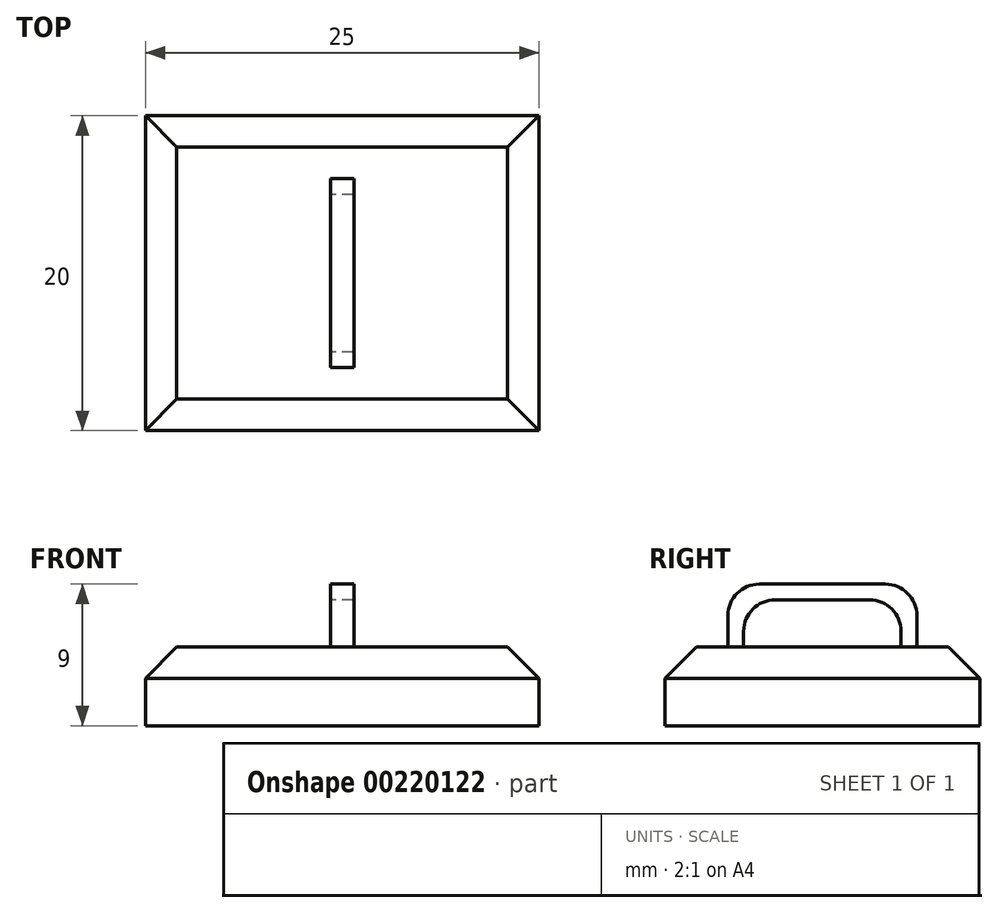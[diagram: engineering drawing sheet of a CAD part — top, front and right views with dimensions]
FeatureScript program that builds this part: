
annotation { "Feature Type Name" : "Feature", "Feature Type Description" : "" }
export const myFeature = defineFeature(function(context is Context, id is Id, definition is map)
    precondition{}
    {
        {
            var Q0;
            Q0=qCreatedBy(makeId("Top.planeOp"),FACE);
            var sketch = newSketch(context, id + "F0", { "sketchPlane" : qUnion([Q0])});
            skLineSegment(sketch, "E0.bottom", {"start": v(12.5, -10) * mm, "end": v(-12.5, -10) * mm});
            skLineSegment(sketch, "E0.top", {"start": v(12.5, 10) * mm, "end": v(-12.5, 10) * mm});
            skLineSegment(sketch, "E0.left", {"start": v(12.5, -10) * mm, "end": v(12.5, 10) * mm});
            skLineSegment(sketch, "E0.right", {"start": v(-12.5, -10) * mm, "end": v(-12.5, 10) * mm});
            skPoint(sketch, "E0.middle", {"position": v(0, 0) * mm});
            skSolve(sketch);
        }
        {
            var Q0;
            Q0 = qSketchRegion(id + "F0", true);
            extrude(context, id + "F1", {"entities" : qUnion([Q0]), "oppositeDirection" : true, "depth" : 5 * mm});
        }
        {
            var Q0;
            Q0=qCreatedBy(makeId("Right.planeOp"),FACE);
            var sketch = newSketch(context, id + "F2", { "sketchPlane" : qUnion([Q0])});
            skLineSegment(sketch, "E1", {"start": v(-6, 0) * mm, "end": v(-6, 4) * mm});
            skLineSegment(sketch, "E2", {"start": v(-5, 3) * mm, "end": v(-5, 0) * mm});
            skLineSegment(sketch, "E3", {"start": v(-5, 0) * mm, "end": v(-6, 0) * mm});
            skLineSegment(sketch, "E4.MirrorCS", {"start": v(6, 0) * mm, "end": v(6, 4) * mm});
            skLineSegment(sketch, "E5.MirrorCS", {"start": v(5, 3) * mm, "end": v(5, 0) * mm});
            skLineSegment(sketch, "E6", {"start": v(-6, 4) * mm, "end": v(6, 4) * mm});
            skLineSegment(sketch, "E7", {"start": v(-5, 3) * mm, "end": v(5, 3) * mm});
            skLineSegment(sketch, "E8", {"start": v(5, 0) * mm, "end": v(6, 0) * mm});
            skSolve(sketch);
        }
        {
            var Q0;
            Q0 = qSketchRegion(id + "F2", true);
            extrude(context, id + "F3", {"entities" : qUnion([Q0]), "operationType" : NewBodyOperationType.ADD, "endBound" : BoundingType.SYMMETRIC, "depth" : 1.5 * mm});
        }
        {
            var Q0;
            Q0=makeQuery(id+"F3.opExtrude","SWEPT_EDGE",EDGE,{"disambiguationData":[OSD([sQuery(id+"F2.wireOp",EDGE,"E2"),sQuery(id+"F2.wireOp",EDGE,"E3")])]});
            var Q1;
            Q1=makeQuery(id+"F3.opExtrude","SWEPT_EDGE",EDGE,{"disambiguationData":[OSD([sQuery(id+"F2.wireOp",EDGE,"E5.MirrorCS"),sQuery(id+"F2.wireOp",EDGE,"E8")])]});
            var Q2;
            Q2=makeQuery(id+"F3.opExtrude","SWEPT_EDGE",EDGE,{"disambiguationData":[OSD([sQuery(id+"F2.wireOp",EDGE,"E1"),sQuery(id+"F2.wireOp",EDGE,"E3")])]});
            var Q3;
            Q3=makeQuery(id+"F3.opExtrude","SWEPT_EDGE",EDGE,{"disambiguationData":[OSD([sQuery(id+"F2.wireOp",EDGE,"E1"),sQuery(id+"F2.wireOp",EDGE,"E6")])]});
            var Q4;
            Q4=makeQuery(id+"F3.opExtrude","SWEPT_EDGE",EDGE,{"disambiguationData":[OSD([sQuery(id+"F2.wireOp",EDGE,"E4.MirrorCS"),sQuery(id+"F2.wireOp",EDGE,"E6")])]});
            var Q5;
            Q5=makeQuery(id+"F3.opExtrude","SWEPT_EDGE",EDGE,{"disambiguationData":[OSD([sQuery(id+"F2.wireOp",EDGE,"E4.MirrorCS"),sQuery(id+"F2.wireOp",EDGE,"E8")])]});
            var Q6;
            Q6=makeQuery(id+"F3.opExtrude","SWEPT_EDGE",EDGE,{"disambiguationData":[OSD([sQuery(id+"F2.wireOp",EDGE,"E2"),sQuery(id+"F2.wireOp",EDGE,"E7")])]});
            var Q7;
            Q7=makeQuery(id+"F3.opExtrude","SWEPT_EDGE",EDGE,{"disambiguationData":[OSD([sQuery(id+"F2.wireOp",EDGE,"E5.MirrorCS"),sQuery(id+"F2.wireOp",EDGE,"E7")])]});
            fillet(context, id + "F4", {"entities" : qUnion([Q0, Q1, Q2, Q3, Q4, Q5, Q6, Q7]), "radius" : 2 * mm, "tangentPropagation" : true, "allowEdgeOverflow" : false});
        }
        {
            var Q0;
            Q0=makeQuery(id+"F1.opExtrude","CAP_EDGE",EDGE,{"disambiguationData":[OSD([sQuery(id+"F0.wireOp",EDGE,"E0.left")])],"isStart":true});
            var Q1;
            Q1=makeQuery(id+"F1.opExtrude","CAP_EDGE",EDGE,{"disambiguationData":[OSD([sQuery(id+"F0.wireOp",EDGE,"E0.bottom")])],"isStart":true});
            var Q2;
            Q2=makeQuery(id+"F1.opExtrude","CAP_EDGE",EDGE,{"disambiguationData":[OSD([sQuery(id+"F0.wireOp",EDGE,"E0.top")])],"isStart":true});
            var Q3;
            Q3=makeQuery(id+"F1.opExtrude","CAP_EDGE",EDGE,{"disambiguationData":[OSD([sQuery(id+"F0.wireOp",EDGE,"E0.right")])],"isStart":true});
            chamfer(context, id + "F5", {"entities" : qUnion([Q0, Q1, Q2, Q3]), "width" : 2 * mm, "tangentPropagation" : true});
        }
    });
